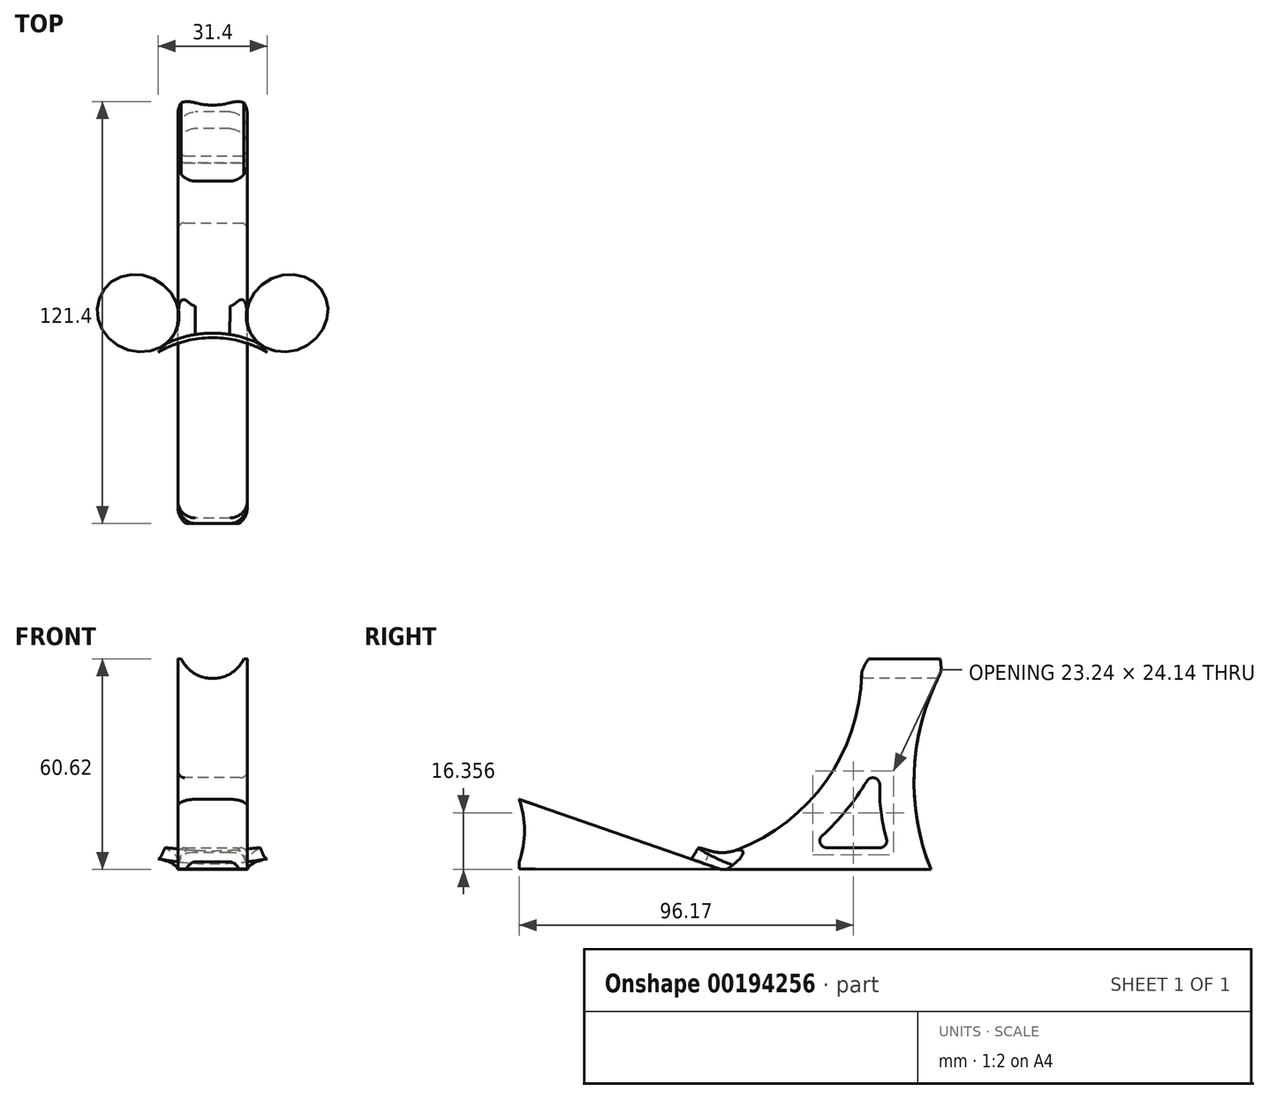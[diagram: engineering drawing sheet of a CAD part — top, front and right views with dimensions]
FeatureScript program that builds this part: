
annotation { "Feature Type Name" : "Feature", "Feature Type Description" : "" }
export const myFeature = defineFeature(function(context is Context, id is Id, definition is map)
    precondition{}
    {
        {
            var Q0;
            Q0=qCreatedBy(makeId("Right.planeOp"),FACE);
            var sketch = newSketch(context, id + "F0", { "sketchPlane" : qUnion([Q0])});
            skLineSegment(sketch, "E0", {"start": v(-48.44, 17.6) * mm, "end": v(2.24, 0) * mm});
            skLineSegment(sketch, "E1", {"start": v(-48.44, -0.4) * mm, "end": v(-48.45, -2.4) * mm});
            skLineSegment(sketch, "E2", {"start": v(-48.45, -2.4) * mm, "end": v(60.02, -2.6) * mm});
            skArc(sketch, "E3", {"start": v(-48.44, -0.4) * mm, "mid": v(-46.88, 8.6) * mm, "end": v(-48.44, 17.6) * mm});
            skLineSegment(sketch, "E4", {"start": v(60.02, -2.6) * mm, "end": v(70.02, -2.62) * mm});
            skArc(sketch, "E5", {"start": v(75.02, 58) * mm, "mid": v(65.4, 28.28) * mm, "end": v(70.02, -2.62) * mm});
            skArc(sketch, "E6", {"start": v(2.24, 0) * mm, "mid": v(37.45, 19.68) * mm, "end": v(50.02, 58) * mm});
            skLineSegment(sketch, "E7", {"start": v(50.02, 58) * mm, "end": v(75.02, 58) * mm});
            skSolve(sketch);
        }
        {
            var Q0;
            Q0=qCreatedBy(makeId("Right.planeOp"),FACE);
            var sketch = newSketch(context, id + "F1", { "sketchPlane" : qUnion([Q0])});
            skLineSegment(sketch, "E8", {"start": v(34.65, 3.67) * mm, "end": v(58.06, 3.67) * mm});
            skPoint(sketch, "E9", {"position": v(57.3, 34.54) * mm});
            skArc(sketch, "E10", {"start": v(34.65, 3.67) * mm, "mid": v(48.08, 17.56) * mm, "end": v(57.3, 34.54) * mm});
            skArc(sketch, "E11", {"start": v(57.3, 34.54) * mm, "mid": v(55.31, 19.04) * mm, "end": v(58.06, 3.67) * mm});
            skSolve(sketch);
        }
        {
            var Q0;
            Q0=makeQuery(id+"F0.imprint","IMPRINT",FACE,{"disambiguationData":[TD([[makeQuery(id+"F0.imprint","IMPRINT",EDGE,{"derivedFrom":sQuery(id+"F0.wireOp",EDGE,"E0")}),-1.0]])]});
            extrude(context, id + "F2", {"entities" : qUnion([Q0]), "endBound" : BoundingType.SYMMETRIC, "depth" : 20 * mm});
        }
        {
            var Q0;
            Q0 = qSketchRegion(id + "F1", true);
            extrude(context, id + "F3", {"entities" : qUnion([Q0]), "operationType" : NewBodyOperationType.REMOVE, "endBound" : BoundingType.SYMMETRIC, "oppositeDirection" : true, "depth" : 25 * mm});
        }
        {
            var Q0;
            Q0=makeQuery(id+"F2.opExtrude","CAP_EDGE",EDGE,{"disambiguationData":[OSD([sQuery(id+"F0.wireOp",EDGE,"E5")])],"isStart":false});
            var Q1;
            Q1=makeQuery(id+"F2.opExtrude","CAP_EDGE",EDGE,{"disambiguationData":[OSD([sQuery(id+"F0.wireOp",EDGE,"E5")])],"isStart":true});
            var Q2;
            Q2=makeQuery(id+"F2.opExtrude","CAP_EDGE",EDGE,{"disambiguationData":[OSD([sQuery(id+"F0.wireOp",EDGE,"E6")])],"isStart":true});
            var Q3;
            Q3=makeQuery(id+"F2.opExtrude","CAP_EDGE",EDGE,{"disambiguationData":[OSD([sQuery(id+"F0.wireOp",EDGE,"E3")])],"isStart":true});
            var Q4;
            Q4=makeQuery(id+"F2.opExtrude","CAP_EDGE",EDGE,{"disambiguationData":[OSD([sQuery(id+"F0.wireOp",EDGE,"E3")])],"isStart":false});
            var Q5;
            Q5=makeQuery(id+"F2.opExtrude","CAP_EDGE",EDGE,{"disambiguationData":[OSD([sQuery(id+"F0.wireOp",EDGE,"E6")])],"isStart":false});
            fillet(context, id + "F4", {"entities" : qUnion([Q0, Q1, Q2, Q3, Q4, Q5]), "radius" : 5 * mm, "tangentPropagation" : true, "allowEdgeOverflow" : false});
        }
        {
            var Q0;
            Q0=makeQuery(id+"F3.boolean.opBoolean","COPY",FACE,{"derivedFrom":makeQuery(id+"F3.opExtrude","SWEPT_FACE",FACE,{"disambiguationData":[OSD([sQuery(id+"F1.wireOp",EDGE,"E10")])]})});
            var Q1;
            Q1=makeQuery(id+"F3.boolean.opBoolean","COPY",FACE,{"derivedFrom":makeQuery(id+"F3.opExtrude","SWEPT_FACE",FACE,{"disambiguationData":[OSD([sQuery(id+"F1.wireOp",EDGE,"E11")])]})});
            var Q2;
            Q2=makeQuery(id+"F3.boolean.opBoolean","COPY",FACE,{"derivedFrom":makeQuery(id+"F3.opExtrude","SWEPT_FACE",FACE,{"disambiguationData":[OSD([sQuery(id+"F1.wireOp",EDGE,"E8")])]})});
            fillet(context, id + "F5", {"entities" : qUnion([Q0, Q1, Q2]), "radius" : 2 * mm, "tangentPropagation" : true, "allowEdgeOverflow" : false});
        }
        {
            var Q0;
            Q0=qCreatedBy(makeId("Right.planeOp"),FACE);
            var sketch = newSketch(context, id + "F6", { "sketchPlane" : qUnion([Q0])});
            skPoint(sketch, "E12", {"position": v(-22.01, 12.66) * mm});
            skLineSegment(sketch, "E13", {"start": v(-22.01, 12.66) * mm, "end": v(-22.67, 10.77) * mm});
            skArc(sketch, "E14", {"start": v(-22.67, 10.77) * mm, "mid": v(-8.44, 6.27) * mm, "end": v(6.1, 2.9) * mm});
            skLineSegment(sketch, "E15", {"start": v(-22.01, 12.66) * mm, "end": v(6.1, 2.9) * mm});
            skSolve(sketch);
        }
        {
            var Q0;
            Q0=makeQuery(id+"F2.opExtrude","SWEPT_FACE",FACE,{"disambiguationData":[OSD([sQuery(id+"F0.wireOp",EDGE,"E0")])]});
            var sketch = newSketch(context, id + "F7", { "sketchPlane" : qUnion([Q0])});
            skPoint(sketch, "E16.0", {"position": v(0, -24.95) * mm});
            skLineSegment(sketch, "E17", {"start": v(0, -24.95) * mm, "end": v(0, 5.05) * mm});
            skLineSegment(sketch, "E18", {"start": v(0, -24.95) * mm, "end": v(0, -54.95) * mm});
            skPoint(sketch, "E18.endSnap0", {"position": v(0, -51.53) * mm});
            skSolve(sketch);
        }
        {
            var Q0;
            Q0=qCreatedBy(makeId("Right.planeOp"),FACE);
            var sketch = newSketch(context, id + "F8", { "sketchPlane" : qUnion([Q0])});
            skPoint(sketch, "E19.0", {"position": v(5.02, -0.96) * mm});
            skPoint(sketch, "E20.0", {"position": v(6.1, 2.9) * mm});
            skPoint(sketch, "E21.0", {"position": v(-23.33, 8.88) * mm});
            skPoint(sketch, "E22.0", {"position": v(-22.67, 10.77) * mm});
            skLineSegment(sketch, "E23", {"start": v(-23.33, 8.88) * mm, "end": v(5.02, -0.96) * mm});
            skLineSegment(sketch, "E24", {"start": v(5.02, -0.96) * mm, "end": v(6.1, 2.9) * mm});
            skLineSegment(sketch, "E25", {"start": v(-22.67, 10.77) * mm, "end": v(-23.33, 8.88) * mm});
            skArc(sketch, "E26", {"start": v(-22.67, 10.77) * mm, "mid": v(-8.44, 6.27) * mm, "end": v(6.1, 2.9) * mm});
            skSolve(sketch);
        }
        {
            var Q0;
            Q0 = qSketchRegion(id + "F8", true);
            var Q1;
            Q1=sQuery(id+"F8.wireOp",EDGE,"E25");
            revolve(context, id + "F9", {"operationType" : NewBodyOperationType.ADD, "entities" : qUnion([Q0]), "axis" : qUnion([Q1]), "revolveType" : RevolveType.FULL});
        }
        {
            var Q0;
            Q0=makeQuery(id+"F9.boolean.opBoolean","INTERSECT",EDGE,{"derivedFrom":[makeQuery(id+"F2.opExtrude","SWEPT_FACE",FACE,{"disambiguationData":[OSD([sQuery(id+"F0.wireOp",EDGE,"E6")])]}),makeQuery(id+"F9.opRevolve","SWEPT_FACE",FACE,{"disambiguationData":[OSD([sQuery(id+"F8.wireOp",EDGE,"E24")])]})]});
            fillet(context, id + "F10", {"entities" : qUnion([Q0]), "radius" : 12 * mm, "tangentPropagation" : true, "allowEdgeOverflow" : false});
        }
        {
            var Q0;
            Q0=qCreatedBy(makeId("Front.planeOp"),FACE);
            var sketch = newSketch(context, id + "F11", { "sketchPlane" : qUnion([Q0])});
            skPoint(sketch, "E27.0", {"position": v(0, 58) * mm});
            skLineSegment(sketch, "E28", {"start": v(0, 58) * mm, "end": v(-9, 58) * mm});
            skLineSegment(sketch, "E29", {"start": v(0, 58) * mm, "end": v(9, 58) * mm});
            skArc(sketch, "E30", {"start": v(-9, 58) * mm, "mid": v(0, 52.36) * mm, "end": v(9, 58) * mm});
            skSolve(sketch);
        }
        {
            var Q0;
            Q0=makeQuery(id+"F11.imprint","IMPRINT",FACE,{"disambiguationData":[TD([[makeQuery(id+"F11.imprint","IMPRINT",EDGE,{"derivedFrom":sQuery(id+"F11.wireOp",EDGE,"E28")}),1.0]])]});
            extrude(context, id + "F12", {"entities" : qUnion([Q0]), "operationType" : NewBodyOperationType.REMOVE, "oppositeDirection" : true, "depth" : 78.3 * mm});
        }
        {
            var Q0;
            Q0=makeQuery(id+"F9.opRevolve","SWEPT_FACE",FACE,{"disambiguationData":[OSD([sQuery(id+"F8.wireOp",EDGE,"E23")])]});
            var sketch = newSketch(context, id + "F13", { "sketchPlane" : qUnion([Q0])});
            skPoint(sketch, "E31.0", {"position": v(0, 24.95) * mm});
            skCircle(sketch, "E32", {"center": v(0, 24.95) * mm, "radius": 30 * mm});
            skSolve(sketch);
        }
        {
            var Q0;
            Q0 = qSketchRegion(id + "F13", true);
            extrude(context, id + "F14", {"entities" : qUnion([Q0]), "operationType" : NewBodyOperationType.REMOVE, "oppositeDirection" : true, "depth" : 5 * mm});
        }
    });
